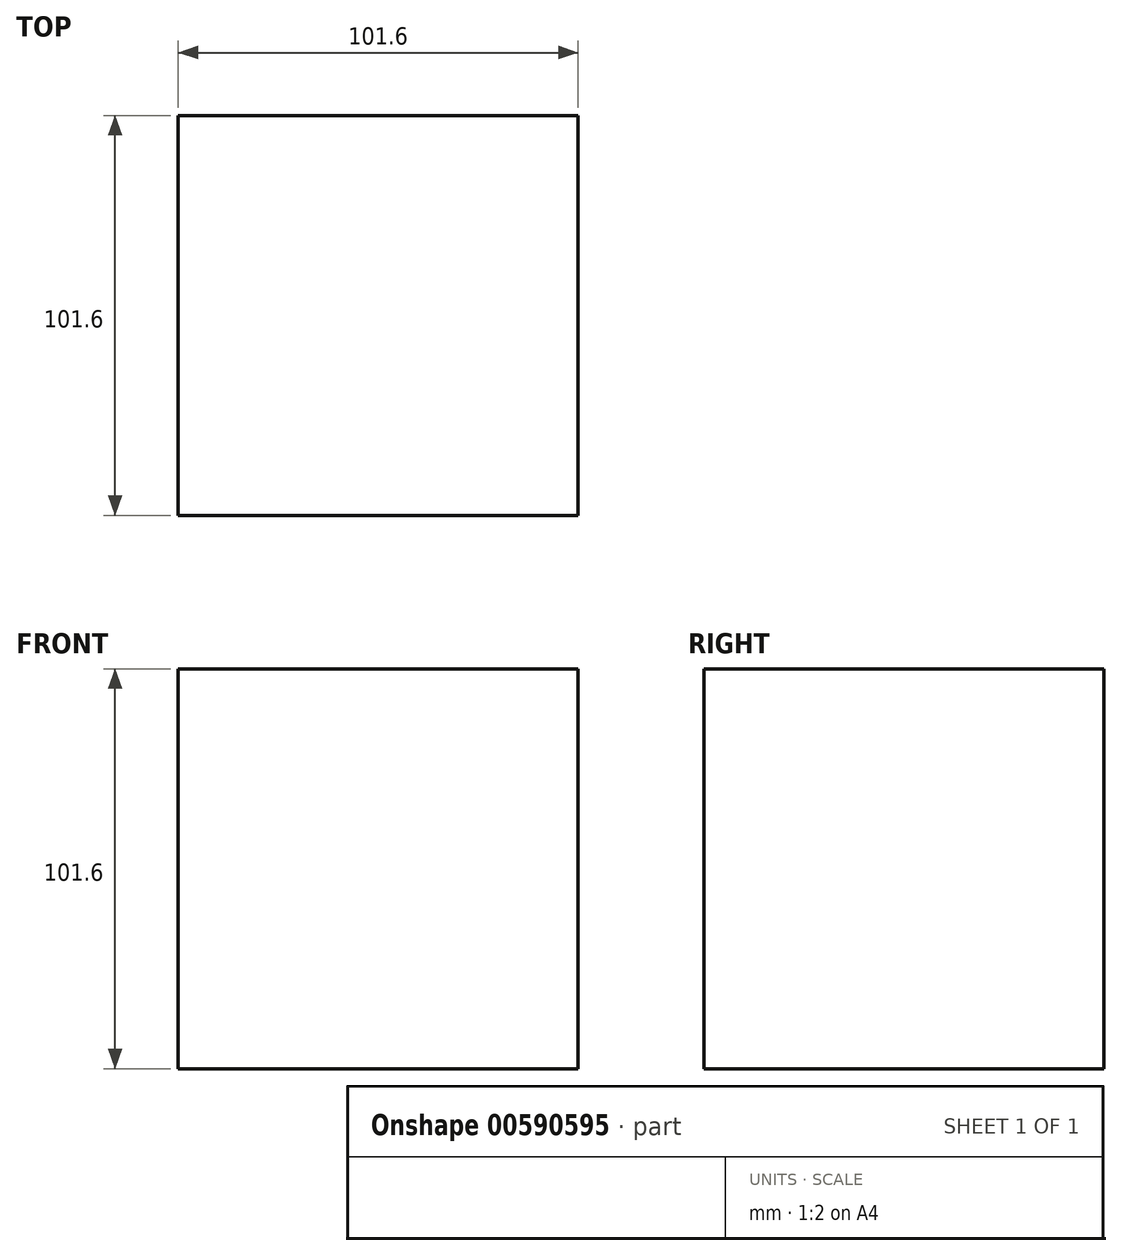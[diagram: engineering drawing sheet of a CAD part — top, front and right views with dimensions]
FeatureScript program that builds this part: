
annotation { "Feature Type Name" : "Feature", "Feature Type Description" : "" }
export const myFeature = defineFeature(function(context is Context, id is Id, definition is map)
    precondition{}
    {
        {
            var Q0;
            Q0=qCreatedBy(makeId("Top.planeOp"),FACE);
            var sketch = newSketch(context, id + "F0", { "sketchPlane" : qUnion([Q0])});
            skLineSegment(sketch, "E0.bottom", {"start": v(0, 0) * mm, "end": v(-101.6, 0) * mm});
            skLineSegment(sketch, "E0.top", {"start": v(0, -101.6) * mm, "end": v(-101.6, -101.6) * mm});
            skLineSegment(sketch, "E0.left", {"start": v(0, 0) * mm, "end": v(0, -101.6) * mm});
            skLineSegment(sketch, "E0.right", {"start": v(-101.6, 0) * mm, "end": v(-101.6, -101.6) * mm});
            skSolve(sketch);
        }
        {
            var Q0;
            Q0 = qSketchRegion(id + "F0", true);
            extrude(context, id + "F1", {"entities" : qUnion([Q0]), "depth" : 101.6 * mm, "offsetDistance" : 25.4 * mm});
        }
    });
